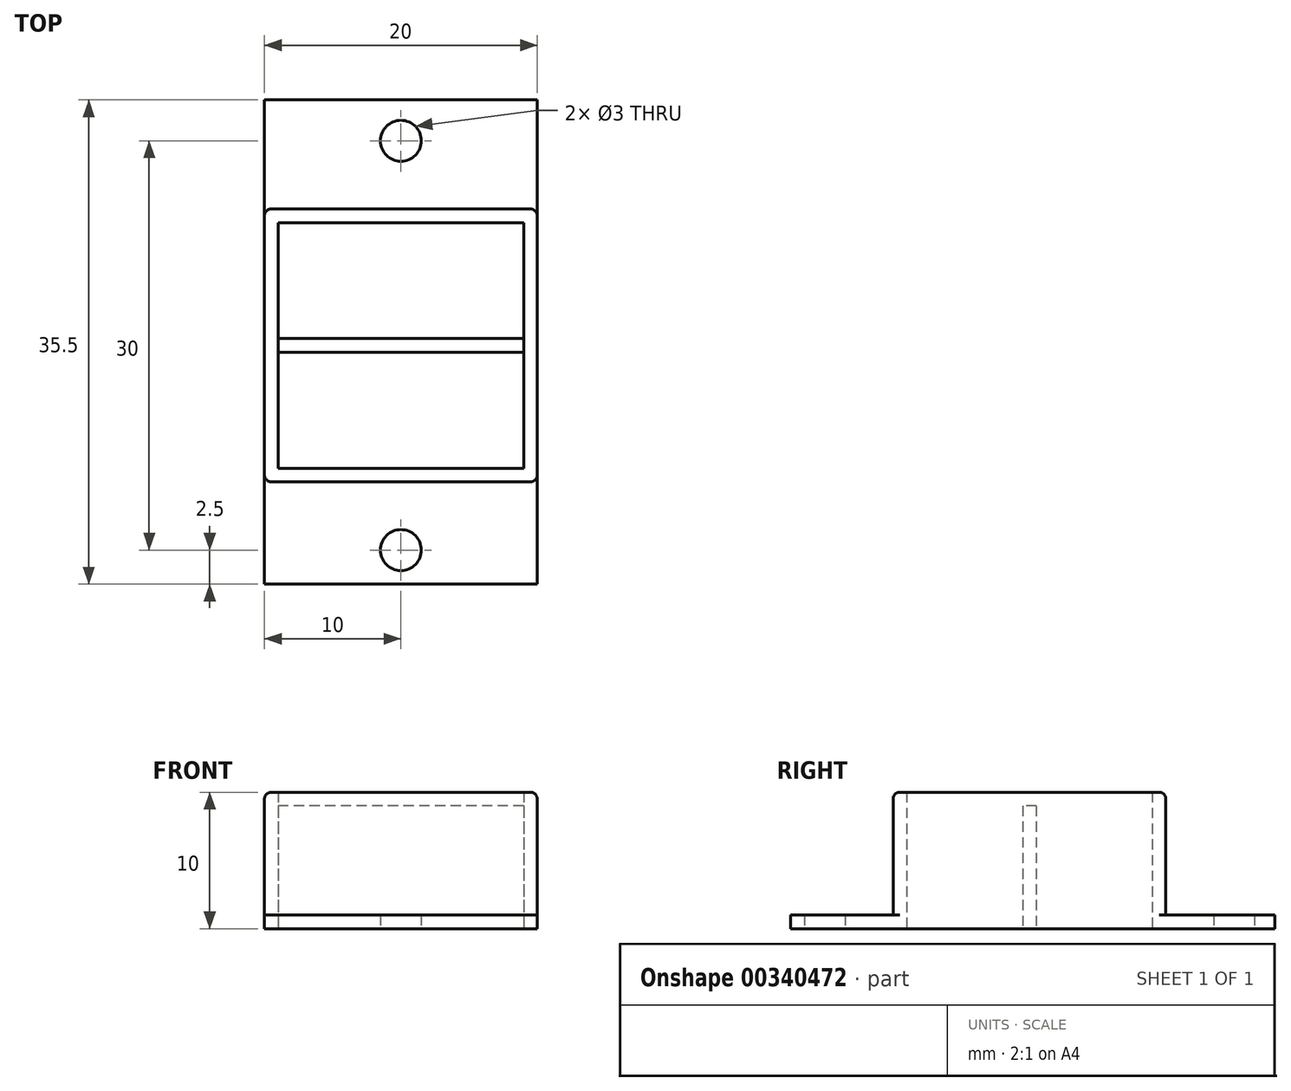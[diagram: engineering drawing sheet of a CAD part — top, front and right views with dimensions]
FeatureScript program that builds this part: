
annotation { "Feature Type Name" : "Feature", "Feature Type Description" : "" }
export const myFeature = defineFeature(function(context is Context, id is Id, definition is map)
    precondition{}
    {
        {
            var Q0;
            Q0=qCreatedBy(makeId("Top.planeOp"),FACE);
            var sketch = newSketch(context, id + "F0", { "sketchPlane" : qUnion([Q0])});
            skPoint(sketch, "E0.middle", {"position": v(0, 0) * mm});
            skLineSegment(sketch, "E1.bottom", {"start": v(10, -10) * mm, "end": v(-10, -10) * mm});
            skLineSegment(sketch, "E1.top", {"start": v(10, 10) * mm, "end": v(-10, 10) * mm});
            skLineSegment(sketch, "E1.left", {"start": v(10, -10) * mm, "end": v(10, 10) * mm});
            skLineSegment(sketch, "E1.right", {"start": v(-10, -10) * mm, "end": v(-10, 10) * mm});
            skSolve(sketch);
        }
        {
            var Q0;
            Q0=makeQuery(id+"F0.imprint","IMPRINT",FACE,{"disambiguationData":[TD([[makeQuery(id+"F0.imprint","IMPRINT",EDGE,{"derivedFrom":sQuery(id+"F0.wireOp",EDGE,"E1.bottom")}),-1.0]])]});
            extrude(context, id + "F1", {"entities" : qUnion([Q0]), "depth" : 10 * mm});
        }
        {
            var Q0;
            Q0=makeQuery(id+"F1.opExtrude","CAP_FACE",FACE,{"disambiguationData":[OSD([sQuery(id+"F0.wireOp",EDGE,"E1.bottom"),sQuery(id+"F0.wireOp",EDGE,"E1.top"),sQuery(id+"F0.wireOp",EDGE,"E1.left"),sQuery(id+"F0.wireOp",EDGE,"E1.right")])],"isStart":true});
            shell(context, id + "F2", {"entities" : qUnion([Q0]), "thickness" : 1 * mm});
        }
        {
            var Q0;
            Q0=qCreatedBy(makeId("Top.planeOp"),FACE);
            var sketch = newSketch(context, id + "F3", { "sketchPlane" : qUnion([Q0])});
            skLineSegment(sketch, "E2.bottom", {"start": v(9, 0.5) * mm, "end": v(0.5, 0.5) * mm});
            skLineSegment(sketch, "E2.top", {"start": v(9, -0.5) * mm, "end": v(0.5, -0.5) * mm});
            skLineSegment(sketch, "E2.left", {"start": v(9, 0.5) * mm, "end": v(9, -0.5) * mm});
            skLineSegment(sketch, "E2.right", {"start": v(-9, 0.5) * mm, "end": v(-9, -0.5) * mm});
            skLineSegment(sketch, "E3.trimOffspring", {"start": v(-0.5, -0.5) * mm, "end": v(-9, -0.5) * mm});
            skLineSegment(sketch, "E4.trimOffspring", {"start": v(-0.5, 0.5) * mm, "end": v(-9, 0.5) * mm});
            skLineSegment(sketch, "E5", {"start": v(-0.5, -0.5) * mm, "end": v(0.5, -0.5) * mm});
            skLineSegment(sketch, "E6", {"start": v(-0.5, 0.5) * mm, "end": v(0.5, 0.5) * mm});
            skSolve(sketch);
        }
        {
            var Q0;
            Q0=qSketchRegion(id+"F3",true);
            extrude(context, id + "F4", {"entities" : qUnion([Q0]), "operationType" : NewBodyOperationType.ADD, "depth" : 9 * mm});
        }
        {
            var Q0;
            Q0=qCreatedBy(makeId("Top.planeOp"),FACE);
            var sketch = newSketch(context, id + "F5", { "sketchPlane" : qUnion([Q0])});
            skLineSegment(sketch, "E7.bottom", {"start": v(-10, -9.5) * mm, "end": v(10, -9.5) * mm});
            skLineSegment(sketch, "E7.top", {"start": v(-10, -17.5) * mm, "end": v(10, -17.5) * mm});
            skLineSegment(sketch, "E7.left", {"start": v(-10, -9.5) * mm, "end": v(-10, -17.5) * mm});
            skLineSegment(sketch, "E7.right", {"start": v(10, -9.5) * mm, "end": v(10, -17.5) * mm});
            skLineSegment(sketch, "E8.bottom", {"start": v(-10, 10) * mm, "end": v(10, 10) * mm});
            skLineSegment(sketch, "E8.top", {"start": v(-10, 18) * mm, "end": v(10, 18) * mm});
            skLineSegment(sketch, "E8.left", {"start": v(-10, 10) * mm, "end": v(-10, 18) * mm});
            skLineSegment(sketch, "E8.right", {"start": v(10, 10) * mm, "end": v(10, 18) * mm});
            skLineSegment(sketch, "E9.bottom", {"start": v(-10, -9.5) * mm, "end": v(-13, -9.5) * mm, "construction": true});
            skLineSegment(sketch, "E9.top", {"start": v(-10, 10) * mm, "end": v(-13, 10) * mm, "construction": true});
            skLineSegment(sketch, "E9.left", {"start": v(-10, -9.5) * mm, "end": v(-10, 10) * mm});
            skLineSegment(sketch, "E9.right", {"start": v(-13, -9.5) * mm, "end": v(-13, 10) * mm, "construction": true});
            skLineSegment(sketch, "E10.bottom", {"start": v(10, -9.5) * mm, "end": v(13, -9.5) * mm, "construction": true});
            skLineSegment(sketch, "E10.top", {"start": v(10, 10) * mm, "end": v(13, 10) * mm, "construction": true});
            skLineSegment(sketch, "E10.left", {"start": v(10, -9.5) * mm, "end": v(10, 10) * mm});
            skLineSegment(sketch, "E10.right", {"start": v(13, -9.5) * mm, "end": v(13, 10) * mm, "construction": true});
            skCircle(sketch, "E11", {"center": v(0, 15) * mm, "radius": 1.5 * mm});
            skCircle(sketch, "E12", {"center": v(0, -15) * mm, "radius": 1.5 * mm});
            skSolve(sketch);
        }
        {
            var Q0;
            Q0=makeQuery(id+"F5.imprint","IMPRINT",FACE,{"disambiguationData":[TD([[makeQuery(id+"F5.imprint","IMPRINT",EDGE,{"derivedFrom":sQuery(id+"F5.wireOp",EDGE,"E9.bottom")}),-1.0]])]});
            var Q1;
            Q1=makeQuery(id+"F5.imprint","IMPRINT",FACE,{"disambiguationData":[TD([[makeQuery(id+"F5.imprint","IMPRINT",EDGE,{"derivedFrom":sQuery(id+"F5.wireOp",EDGE,"E7.bottom")}),-1.0]])]});
            var Q2;
            Q2=makeQuery(id+"F5.imprint","IMPRINT",FACE,{"disambiguationData":[TD([[makeQuery(id+"F5.imprint","IMPRINT",EDGE,{"derivedFrom":sQuery(id+"F5.wireOp",EDGE,"E10.bottom")}),1.0]])]});
            var Q3;
            Q3=makeQuery(id+"F5.imprint","IMPRINT",FACE,{"disambiguationData":[TD([[makeQuery(id+"F5.imprint","IMPRINT",EDGE,{"derivedFrom":sQuery(id+"F5.wireOp",EDGE,"E8.bottom")}),1.0]])]});
            extrude(context, id + "F6", {"entities" : qUnion([Q0, Q1, Q2, Q3]), "operationType" : NewBodyOperationType.ADD, "depth" : 1 * mm});
        }
        {
            var Q0;
            Q0=makeQuery(id+"F1.opExtrude","CAP_FACE",FACE,{"disambiguationData":[OSD([sQuery(id+"F0.wireOp",EDGE,"E1.bottom"),sQuery(id+"F0.wireOp",EDGE,"E1.top"),sQuery(id+"F0.wireOp",EDGE,"E1.left"),sQuery(id+"F0.wireOp",EDGE,"E1.right")])],"isStart":false});
            var sketch = newSketch(context, id + "F7", { "sketchPlane" : qUnion([Q0])});
            skLineSegment(sketch, "E13.bottom", {"start": v(9, 9) * mm, "end": v(-9, 9) * mm});
            skLineSegment(sketch, "E13.top", {"start": v(9, -9) * mm, "end": v(-9, -9) * mm});
            skLineSegment(sketch, "E13.left", {"start": v(9, 9) * mm, "end": v(9, -9) * mm});
            skLineSegment(sketch, "E13.right", {"start": v(-9, 9) * mm, "end": v(-9, -9) * mm});
            skPoint(sketch, "E13.middle", {"position": v(0, 0) * mm});
            skSolve(sketch);
        }
        {
            var Q0;
            Q0=qSketchRegion(id+"F7",true);
            extrude(context, id + "F8", {"entities" : qUnion([Q0]), "operationType" : NewBodyOperationType.REMOVE, "oppositeDirection" : true, "depth" : 1 * mm});
        }
        {
            var Q0;
            Q0=makeQuery(id+"F1.opExtrude","SWEPT_EDGE",EDGE,{"disambiguationData":[OSD([sQuery(id+"F0.wireOp",EDGE,"E1.bottom"),sQuery(id+"F0.wireOp",EDGE,"E1.right")])]});
            var Q1;
            Q1=makeQuery(id+"F1.opExtrude","SWEPT_EDGE",EDGE,{"disambiguationData":[OSD([sQuery(id+"F0.wireOp",EDGE,"E1.bottom"),sQuery(id+"F0.wireOp",EDGE,"E1.left")])]});
            var Q2;
            Q2=makeQuery(id+"F1.opExtrude","CAP_EDGE",EDGE,{"disambiguationData":[OSD([sQuery(id+"F0.wireOp",EDGE,"E1.bottom")])],"isStart":false});
            var Q3;
            Q3=makeQuery(id+"F1.opExtrude","CAP_EDGE",EDGE,{"disambiguationData":[OSD([sQuery(id+"F0.wireOp",EDGE,"E1.left")])],"isStart":false});
            var Q4;
            Q4=makeQuery(id+"F1.opExtrude","CAP_EDGE",EDGE,{"disambiguationData":[OSD([sQuery(id+"F0.wireOp",EDGE,"E1.right")])],"isStart":false});
            var Q5;
            Q5=makeQuery(id+"F1.opExtrude","SWEPT_EDGE",EDGE,{"disambiguationData":[OSD([sQuery(id+"F0.wireOp",EDGE,"E1.top"),sQuery(id+"F0.wireOp",EDGE,"E1.left")])]});
            var Q6;
            Q6=makeQuery(id+"F1.opExtrude","SWEPT_EDGE",EDGE,{"disambiguationData":[OSD([sQuery(id+"F0.wireOp",EDGE,"E1.top"),sQuery(id+"F0.wireOp",EDGE,"E1.right")])]});
            var Q7;
            Q7=makeQuery(id+"F1.opExtrude","CAP_EDGE",EDGE,{"disambiguationData":[OSD([sQuery(id+"F0.wireOp",EDGE,"E1.top")])],"isStart":false});
            fillet(context, id + "F9", {"entities" : qUnion([Q0, Q1, Q2, Q3, Q4, Q5, Q6, Q7]), "radius" : 0.5 * mm, "tangentPropagation" : true, "allowEdgeOverflow" : false});
        }
    });
